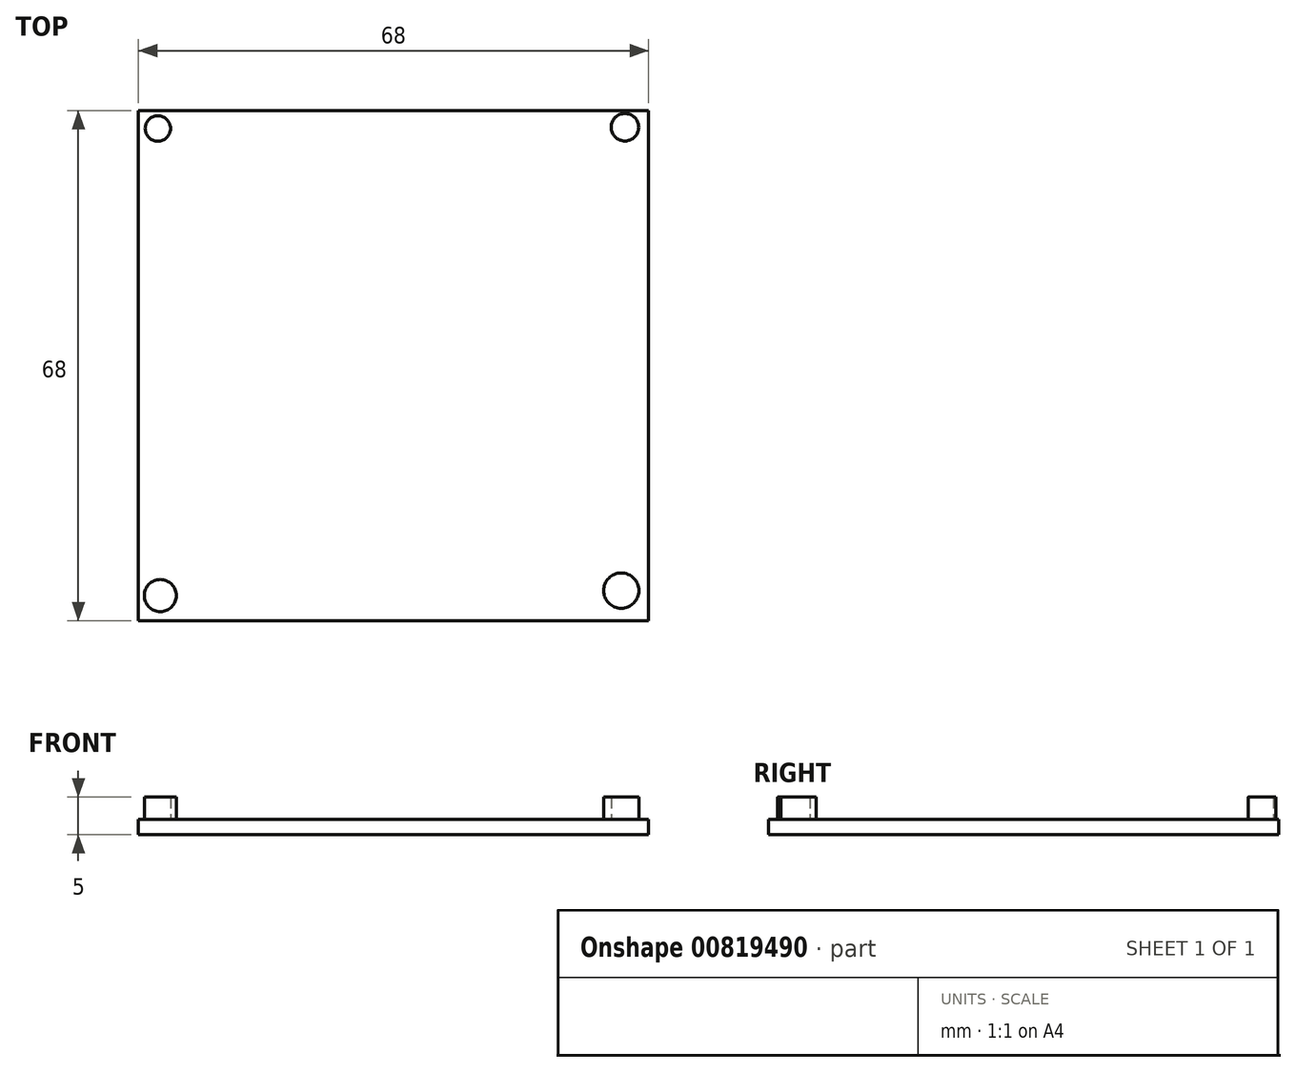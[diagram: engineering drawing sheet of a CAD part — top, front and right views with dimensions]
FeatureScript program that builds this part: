
annotation { "Feature Type Name" : "Feature", "Feature Type Description" : "" }
export const myFeature = defineFeature(function(context is Context, id is Id, definition is map)
    precondition{}
    {
        {
            var Q0;
            Q0=qCreatedBy(makeId("Top.planeOp"),FACE);
            var sketch = newSketch(context, id + "F0", { "sketchPlane" : qUnion([Q0])});
            skLineSegment(sketch, "E0.bottom", {"start": v(34, -34) * mm, "end": v(-34, -34) * mm});
            skLineSegment(sketch, "E0.top", {"start": v(34, 34) * mm, "end": v(-34, 34) * mm});
            skLineSegment(sketch, "E0.left", {"start": v(34, -34) * mm, "end": v(34, 34) * mm});
            skLineSegment(sketch, "E0.right", {"start": v(-34, -34) * mm, "end": v(-34, 34) * mm});
            skPoint(sketch, "E0.middle", {"position": v(0, 0) * mm});
            skSolve(sketch);
        }
        {
            var Q0;
            Q0=makeQuery(id+"F0.imprint","IMPRINT",FACE,{"disambiguationData":[TD([[makeQuery(id+"F0.imprint","IMPRINT",EDGE,{"derivedFrom":sQuery(id+"F0.wireOp",EDGE,"E0.bottom")}),-1.0]])]});
            extrude(context, id + "F1", {"entities" : qUnion([Q0]), "depth" : 2 * mm, "offsetDistance" : 25 * mm});
        }
        {
            var Q0;
            Q0=makeQuery(id+"F1.opExtrude","CAP_FACE",FACE,{"disambiguationData":[OSD([sQuery(id+"F0.wireOp",EDGE,"E0.bottom"),sQuery(id+"F0.wireOp",EDGE,"E0.top"),sQuery(id+"F0.wireOp",EDGE,"E0.left"),sQuery(id+"F0.wireOp",EDGE,"E0.right")])],"isStart":false});
            var sketch = newSketch(context, id + "F2", { "sketchPlane" : qUnion([Q0])});
            skCircle(sketch, "E1", {"center": v(-31.41, 31.62) * mm, "radius": 1.7 * mm});
            skCircle(sketch, "E2", {"center": v(30.85, 31.79) * mm, "radius": 1.84 * mm});
            skCircle(sketch, "E3", {"center": v(-31.09, -30.65) * mm, "radius": 2.14 * mm});
            skCircle(sketch, "E4", {"center": v(30.36, -29.99) * mm, "radius": 2.35 * mm});
            skSolve(sketch);
        }
        {
            var Q0;
            Q0=makeQuery(id+"F2.imprint","IMPRINT",FACE,{"disambiguationData":[TD([[makeQuery(id+"F2.imprint","IMPRINT",EDGE,{"derivedFrom":sQuery(id+"F2.wireOp",EDGE,"E1")}),1.0]])]});
            var Q1;
            Q1=makeQuery(id+"F2.imprint","IMPRINT",FACE,{"disambiguationData":[TD([[makeQuery(id+"F2.imprint","IMPRINT",EDGE,{"derivedFrom":sQuery(id+"F2.wireOp",EDGE,"E2")}),1.0]])]});
            var Q2;
            Q2=makeQuery(id+"F2.imprint","IMPRINT",FACE,{"disambiguationData":[TD([[makeQuery(id+"F2.imprint","IMPRINT",EDGE,{"derivedFrom":sQuery(id+"F2.wireOp",EDGE,"E4")}),1.0]])]});
            var Q3;
            Q3=makeQuery(id+"F2.imprint","IMPRINT",FACE,{"disambiguationData":[TD([[makeQuery(id+"F2.imprint","IMPRINT",EDGE,{"derivedFrom":sQuery(id+"F2.wireOp",EDGE,"E3")}),1.0]])]});
            extrude(context, id + "F3", {"entities" : qUnion([Q0, Q1, Q2, Q3]), "operationType" : NewBodyOperationType.ADD, "depth" : 3 * mm, "offsetDistance" : 25 * mm});
        }
    });
